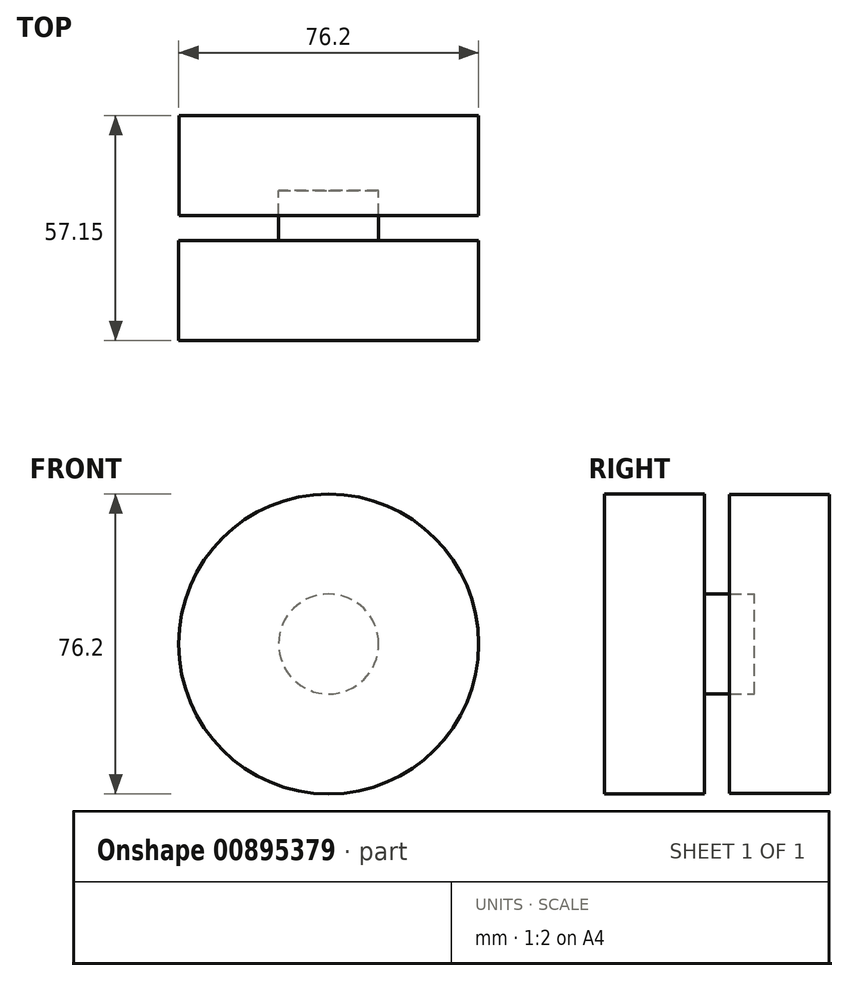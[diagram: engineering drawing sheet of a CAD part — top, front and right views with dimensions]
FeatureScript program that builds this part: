
annotation { "Feature Type Name" : "Feature", "Feature Type Description" : "" }
export const myFeature = defineFeature(function(context is Context, id is Id, definition is map)
    precondition{}
    {
        {
            var Q0;
            Q0=qCreatedBy(makeId("Front.planeOp"),FACE);
            var sketch = newSketch(context, id + "F0", { "sketchPlane" : qUnion([Q0])});
            skCircle(sketch, "E0", {"center": v(0, 0) * mm, "radius": 38 * mm});
            skSolve(sketch);
        }
        {
            var Q0;
            Q0=makeQuery(id+"F0.imprint","IMPRINT",FACE,{"disambiguationData":[TD([[makeQuery(id+"F0.imprint","IMPRINT",EDGE,{"derivedFrom":sQuery(id+"F0.wireOp",EDGE,"E0")}),1.0]])]});
            extrude(context, id + "F1", {"entities" : qUnion([Q0]), "endBound" : BoundingType.SYMMETRIC, "depth" : 25.4 * mm, "offsetDistance" : 25.4 * mm});
        }
        {
            var Q0;
            Q0=makeQuery(id+"F1.opExtrude","CAP_FACE",FACE,{"disambiguationData":[OSD([sQuery(id+"F0.wireOp",EDGE,"E0")])],"isStart":false});
            var sketch = newSketch(context, id + "F2", { "sketchPlane" : qUnion([Q0])});
            skCircle(sketch, "E1", {"center": v(0, 0) * mm, "radius": 12.7 * mm});
            skSolve(sketch);
        }
        {
            var Q0;
            Q0=makeQuery(id+"F2.imprint","IMPRINT",FACE,{"disambiguationData":[TD([[makeQuery(id+"F2.imprint","IMPRINT",EDGE,{"derivedFrom":sQuery(id+"F2.wireOp",EDGE,"E1")}),1.0]])]});
            var Q1;
            Q1=sQuery(id+"F2.wireOp",EDGE,"E1");
            extrude(context, id + "F3", {"entities" : qUnion([Q0]), "surfaceEntities" : qUnion([Q1]), "endBound" : BoundingType.SYMMETRIC, "depth" : 12.7 * mm, "offsetDistance" : 25.4 * mm});
        }
        {
            var Q0;
            Q0=makeQuery(id+"F3.opExtrude","CAP_FACE",FACE,{"disambiguationData":[OSD([sQuery(id+"F2.wireOp",EDGE,"E1")])],"isStart":false});
            var sketch = newSketch(context, id + "F4", { "sketchPlane" : qUnion([Q0])});
            skCircle(sketch, "E2", {"center": v(0, 0) * mm, "radius": 38.1 * mm});
            skSolve(sketch);
        }
        {
            var Q0;
            Q0 = qSketchRegion(id + "F4", true);
            extrude(context, id + "F5", {"entities" : qUnion([Q0]), "operationType" : NewBodyOperationType.ADD, "depth" : 25.4 * mm, "offsetDistance" : 25.4 * mm});
        }
    });
